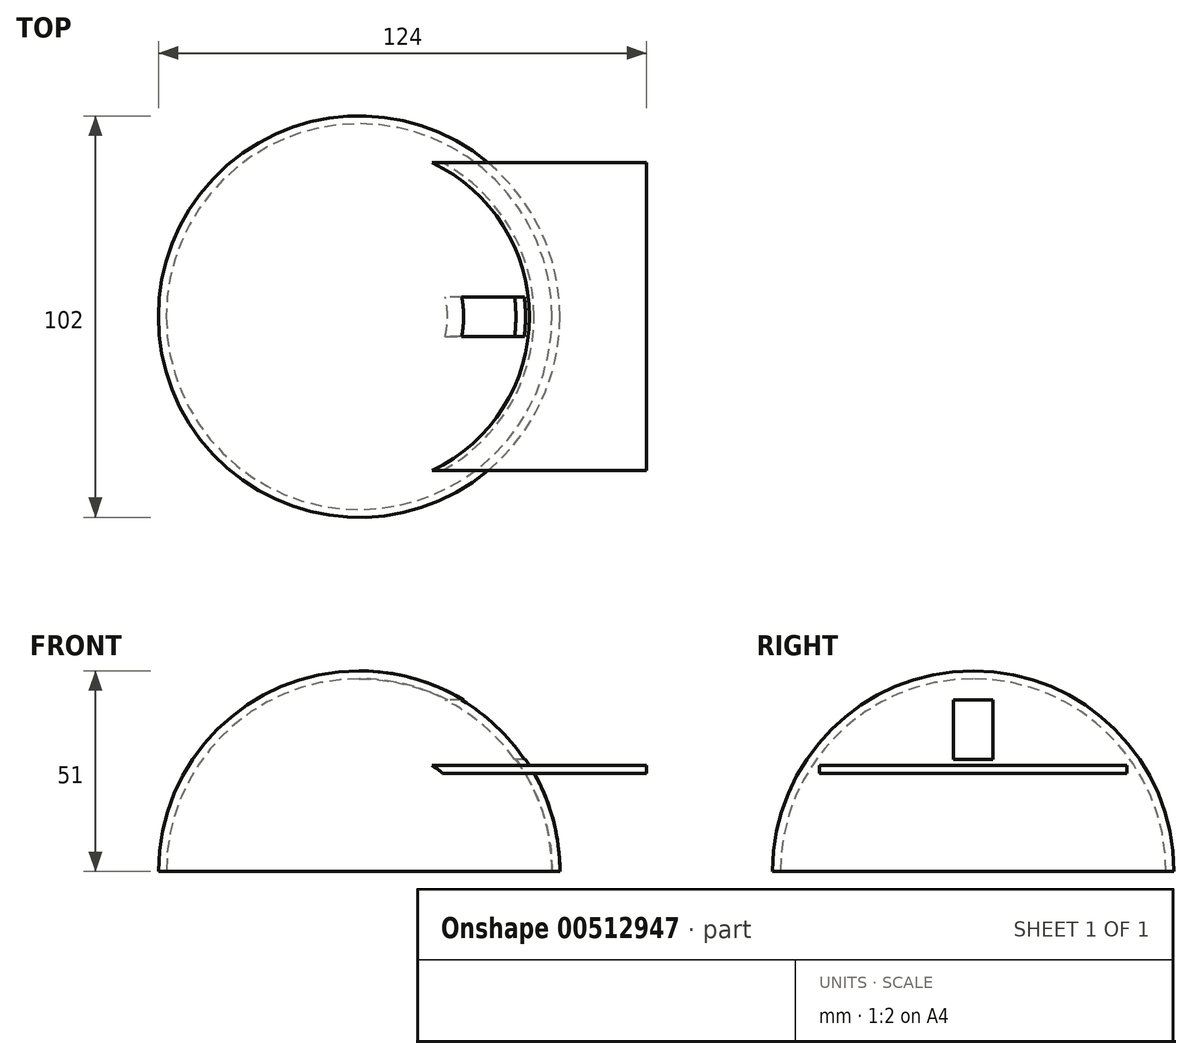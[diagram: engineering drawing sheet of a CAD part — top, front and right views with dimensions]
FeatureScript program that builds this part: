
annotation { "Feature Type Name" : "Feature", "Feature Type Description" : "" }
export const myFeature = defineFeature(function(context is Context, id is Id, definition is map)
    precondition{}
    {
        {
            var Q0;
            Q0=qCreatedBy(makeId("Front.planeOp"),FACE);
            var sketch = newSketch(context, id + "F0", { "sketchPlane" : qUnion([Q0])});
            skArc(sketch, "E0", {"start": v(51, 0) * mm, "mid": v(36.06, 36.06) * mm, "end": v(0, 51) * mm});
            skLineSegment(sketch, "E1", {"start": v(0, 51) * mm, "end": v(0, 0) * mm});
            skLineSegment(sketch, "E2", {"start": v(0, 0) * mm, "end": v(51, 0) * mm});
            skSolve(sketch);
        }
        {
            var Q0;
            Q0=makeQuery(id+"F0.imprint","IMPRINT",FACE,{"disambiguationData":[TD([[makeQuery(id+"F0.imprint","IMPRINT",EDGE,{"derivedFrom":sQuery(id+"F0.wireOp",EDGE,"E0")}),1.0]])]});
            var Q1;
            Q1=sQuery(id+"F0.wireOp",EDGE,"E1");
            revolve(context, id + "F1", {"entities" : qUnion([Q0]), "axis" : qUnion([Q1]), "revolveType" : RevolveType.FULL});
        }
        {
            var Q0;
            Q0=qCreatedBy(makeId("Front.planeOp"),FACE);
            var sketch = newSketch(context, id + "F2", { "sketchPlane" : qUnion([Q0])});
            skArc(sketch, "E3", {"start": v(49, 0) * mm, "mid": v(34.65, 34.65) * mm, "end": v(0, 49) * mm});
            skLineSegment(sketch, "E4", {"start": v(0, 49) * mm, "end": v(0, 0) * mm});
            skLineSegment(sketch, "E5", {"start": v(49, 0) * mm, "end": v(0, 0) * mm});
            skSolve(sketch);
        }
        {
            var Q0;
            Q0=qSketchRegion(id+"F2",true);
            var Q1;
            Q1=sQuery(id+"F2.wireOp",EDGE,"E4");
            revolve(context, id + "F3", {"operationType" : NewBodyOperationType.REMOVE, "entities" : qUnion([Q0]), "axis" : qUnion([Q1]), "revolveType" : RevolveType.FULL, "oppositeDirection" : true});
        }
        {
            var Q0;
            Q0=qCreatedBy(makeId("Front.planeOp"),FACE);
            var sketch = newSketch(context, id + "F4", { "sketchPlane" : qUnion([Q0])});
            skLineSegment(sketch, "E6", {"start": v(0, 0) * mm, "end": v(0, 25) * mm});
            skArc(sketch, "E7", {"start": v(51, 0) * mm, "mid": v(36.06, 36.06) * mm, "end": v(0, 51) * mm});
            skLineSegment(sketch, "E8", {"start": v(44.45, 25) * mm, "end": v(74.45, 25) * mm});
            skLineSegment(sketch, "E9", {"start": v(0, 25) * mm, "end": v(44.45, 25) * mm});
            skLineSegment(sketch, "E10", {"start": v(44.45, 25) * mm, "end": v(44.45, 0) * mm});
            skSolve(sketch);
        }
        {
            var Q0;
            Q0=qCreatedBy(makeId("Top.planeOp"),FACE);
            cPlane(context, id + "F5", {"entities" : qUnion([Q0]), "cplaneType" : CPlaneType.OFFSET, "offset" : 25 * mm, "width" : 150 * mm, "height" : 150 * mm});
        }
        {
            var Q0;
            Q0=qCreatedBy(id+"F5.planeOp",FACE);
            var sketch = newSketch(context, id + "F6", { "sketchPlane" : qUnion([Q0])});
            skPoint(sketch, "E11.0", {"position": v(0, 0) * mm});
            skArc(sketch, "E12", {"start": v(0, -43) * mm, "mid": v(43, 0) * mm, "end": v(0, 43) * mm});
            skLineSegment(sketch, "E13", {"start": v(17.9, 39.1) * mm, "end": v(17.9, -39.1) * mm});
            skLineSegment(sketch, "E14", {"start": v(43, 0) * mm, "end": v(73, 0) * mm});
            skPoint(sketch, "E14.endSnap0", {"position": v(43, 0) * mm});
            skLineSegment(sketch, "E15", {"start": v(73, 0) * mm, "end": v(73, 39.1) * mm});
            skLineSegment(sketch, "E16", {"start": v(17.9, 39.1) * mm, "end": v(73, 39.1) * mm});
            skLineSegment(sketch, "E17", {"start": v(73, 0) * mm, "end": v(73, -39.1) * mm});
            skLineSegment(sketch, "E18", {"start": v(73, -39.1) * mm, "end": v(17.9, -39.1) * mm});
            skSolve(sketch);
        }
        {
            var Q0;
            {var subQ2=sQuery(id+"F6.wireOp",EDGE,"E14");Q0=makeQuery(id+"F6.imprint","IMPRINT",FACE,{"disambiguationData":[TD([[makeQuery(id+"F6.imprint","IMPRINT",EDGE,{"derivedFrom":subQ2}),-1.0]])]});}
            var Q1;
            {var subQ2=sQuery(id+"F6.wireOp",EDGE,"E14");Q1=makeQuery(id+"F6.imprint","IMPRINT",FACE,{"disambiguationData":[TD([[makeQuery(id+"F6.imprint","IMPRINT",EDGE,{"derivedFrom":subQ2}),1.0]])]});}
            extrude(context, id + "F7", {"entities" : qUnion([Q0, Q1]), "operationType" : NewBodyOperationType.ADD, "depth" : 2 * mm, "offsetDistance" : 25 * mm});
        }
        {
            var Q0;
            Q0=qCreatedBy(makeId("Front.planeOp"),FACE);
            var sketch = newSketch(context, id + "F8", { "sketchPlane" : qUnion([Q0])});
            skPoint(sketch, "E19.0", {"position": v(36.06, 36.06) * mm});
            skLineSegment(sketch, "E20", {"start": v(36.06, 36.06) * mm, "end": v(0, 36.06) * mm});
            skLineSegment(sketch, "E21", {"start": v(0, 36.06) * mm, "end": v(0, 43.56) * mm});
            skLineSegment(sketch, "E22", {"start": v(0, 36.06) * mm, "end": v(0, 28.56) * mm});
            skLineSegment(sketch, "E23", {"start": v(0, 43.56) * mm, "end": v(0, 28.56) * mm});
            skSolve(sketch);
        }
        {
            var Q0;
            Q0=qCreatedBy(makeId("Right.planeOp"),FACE);
            var sketch = newSketch(context, id + "F9", { "sketchPlane" : qUnion([Q0])});
            skPoint(sketch, "E24.0", {"position": v(0, 43.56) * mm});
            skPoint(sketch, "E25.0", {"position": v(0, 28.56) * mm});
            skPoint(sketch, "E26.0", {"position": v(0, 36.06) * mm});
            skLineSegment(sketch, "E27", {"start": v(0, 36.06) * mm, "end": v(-5, 36.06) * mm});
            skLineSegment(sketch, "E28", {"start": v(0, 36.06) * mm, "end": v(5, 36.06) * mm});
            skLineSegment(sketch, "E29", {"start": v(0, 43.56) * mm, "end": v(-5, 43.56) * mm});
            skLineSegment(sketch, "E30", {"start": v(-5, 43.56) * mm, "end": v(-5, 28.56) * mm});
            skLineSegment(sketch, "E31", {"start": v(-5, 28.56) * mm, "end": v(5, 28.56) * mm});
            skLineSegment(sketch, "E32", {"start": v(5, 28.56) * mm, "end": v(5, 43.56) * mm});
            skLineSegment(sketch, "E33", {"start": v(5, 43.56) * mm, "end": v(0, 43.56) * mm});
            skSolve(sketch);
        }
        {
            var Q0;
            Q0=qSketchRegion(id+"F9",true);
            var Q1;
            Q1=sQuery(id+"F9.wireOp",EDGE,"E29");
            var Q2;
            Q2=sQuery(id+"F9.wireOp",EDGE,"E33");
            var Q3;
            Q3=sQuery(id+"F9.wireOp",EDGE,"E30");
            var Q4;
            Q4=sQuery(id+"F9.wireOp",EDGE,"E31");
            var Q5;
            Q5=sQuery(id+"F9.wireOp",EDGE,"E32");
            extrude(context, id + "F10", {"entities" : qUnion([Q0]), "operationType" : NewBodyOperationType.REMOVE, "surfaceEntities" : qUnion([Q1, Q2, Q3, Q4, Q5]), "depth" : 64.1 * mm});
        }
    });
